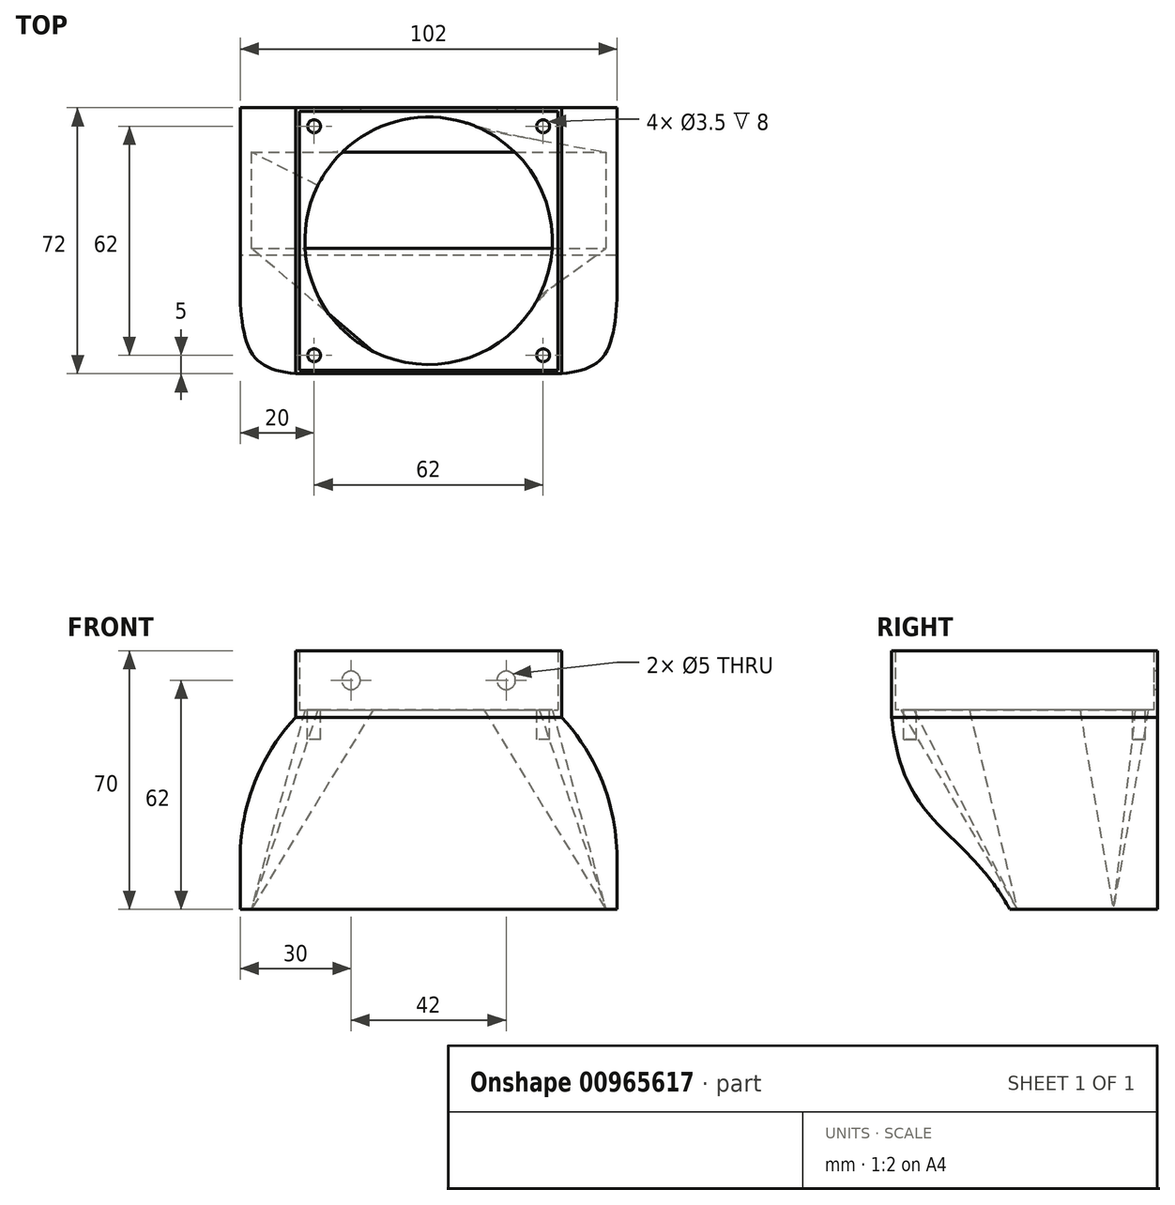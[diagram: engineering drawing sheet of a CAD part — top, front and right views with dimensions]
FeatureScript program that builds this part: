
annotation { "Feature Type Name" : "Feature", "Feature Type Description" : "" }
export const myFeature = defineFeature(function(context is Context, id is Id, definition is map)
    precondition{}
    {
        {
            var Q0;
            Q0=qCreatedBy(makeId("Top.planeOp"),FACE);
            cPlane(context, id + "F0", {"entities" : qUnion([Q0]), "cplaneType" : CPlaneType.OFFSET, "offset" : 70 * mm, "oppositeDirection" : true, "width" : 150 * mm, "height" : 150 * mm});
        }
        {
            var Q0;
            Q0=qCreatedBy(makeId("Top.planeOp"),FACE);
            cPlane(context, id + "F1", {"entities" : qUnion([Q0]), "cplaneType" : CPlaneType.OFFSET, "offset" : 16 * mm, "oppositeDirection" : true, "width" : 150 * mm, "height" : 150 * mm});
        }
        {
            var Q0;
            Q0=qCreatedBy(id+"F1.planeOp",FACE);
            var sketch = newSketch(context, id + "F2", { "sketchPlane" : qUnion([Q0])});
            skCircle(sketch, "E0", {"center": v(0, 0) * mm, "radius": 33.5 * mm});
            skLineSegment(sketch, "E1.bottom", {"start": v(-35, 35) * mm, "end": v(35, 35) * mm});
            skLineSegment(sketch, "E1.top", {"start": v(-35, -35) * mm, "end": v(35, -35) * mm});
            skLineSegment(sketch, "E1.left", {"start": v(-35, 35) * mm, "end": v(-35, -35) * mm});
            skLineSegment(sketch, "E1.right", {"start": v(35, 35) * mm, "end": v(35, -35) * mm});
            skCircle(sketch, "E2", {"center": v(-31, 31) * mm, "radius": 2 * mm});
            skCircle(sketch, "E3", {"center": v(31, 31) * mm, "radius": 2 * mm});
            skCircle(sketch, "E4", {"center": v(31, -31) * mm, "radius": 2 * mm});
            skCircle(sketch, "E5", {"center": v(-31, -31) * mm, "radius": 2 * mm});
            skSolve(sketch);
        }
        {
            var Q0;
            Q0=qCreatedBy(makeId("Top.planeOp"),FACE);
            var sketch = newSketch(context, id + "F3", { "sketchPlane" : qUnion([Q0])});
            skLineSegment(sketch, "E6.bottom", {"start": v(-36, 36) * mm, "end": v(36, 36) * mm});
            skLineSegment(sketch, "E6.top", {"start": v(-36, -36) * mm, "end": v(36, -36) * mm});
            skLineSegment(sketch, "E6.left", {"start": v(-36, 36) * mm, "end": v(-36, -36) * mm});
            skLineSegment(sketch, "E6.right", {"start": v(36, 36) * mm, "end": v(36, -36) * mm});
            skPoint(sketch, "E6.middle", {"position": v(0, 0) * mm});
            skCircle(sketch, "E7", {"center": v(-31, 31) * mm, "radius": 1.75 * mm});
            skCircle(sketch, "E8", {"center": v(31, 31) * mm, "radius": 1.75 * mm});
            skCircle(sketch, "E9", {"center": v(31, -31) * mm, "radius": 1.75 * mm});
            skCircle(sketch, "E10", {"center": v(-31, -31) * mm, "radius": 1.75 * mm});
            skSolve(sketch);
        }
        {
            var Q0;
            Q0=qCreatedBy(id+"F0.planeOp",FACE);
            var sketch = newSketch(context, id + "F4", { "sketchPlane" : qUnion([Q0])});
            skLineSegment(sketch, "E11.bottom", {"start": v(-50, 26) * mm, "end": v(50, 26) * mm});
            skLineSegment(sketch, "E11.top", {"start": v(-50, -4) * mm, "end": v(50, -4) * mm});
            skLineSegment(sketch, "E11.left", {"start": v(-50, 26) * mm, "end": v(-50, -4) * mm});
            skLineSegment(sketch, "E11.right", {"start": v(50, 26) * mm, "end": v(50, -4) * mm});
            skLineSegment(sketch, "E12.bottom", {"start": v(-48, 24) * mm, "end": v(48, 24) * mm});
            skLineSegment(sketch, "E12.top", {"start": v(-48, -2) * mm, "end": v(48, -2) * mm});
            skLineSegment(sketch, "E12.left", {"start": v(-48, 24) * mm, "end": v(-48, -2) * mm});
            skLineSegment(sketch, "E12.right", {"start": v(48, 24) * mm, "end": v(48, -2) * mm});
            skSolve(sketch);
        }
        {
            var Q0;
            Q0=makeQuery(id+"F3.imprint","IMPRINT",FACE,{"disambiguationData":[TD([[makeQuery(id+"F3.imprint","IMPRINT",EDGE,{"derivedFrom":sQuery(id+"F3.wireOp",EDGE,"E6.bottom")}),-1.0]])]});
            extrude(context, id + "F5", {"entities" : qUnion([Q0]), "oppositeDirection" : true, "depth" : 18 * mm, "offsetDistance" : 25 * mm});
        }
        {
            var Q0;
            Q0=qCreatedBy(makeId("Right.planeOp"),FACE);
            var sketch = newSketch(context, id + "F6", { "sketchPlane" : qUnion([Q0])});
            skFitSpline(sketch, "E13", {"points": [v(-4, -70) * mm, v(-36, -18) * mm], "startDerivative": vector(-37.44, 68.12) * mm, "endDerivative": vector(-9.27, 91.12) * mm});
            skLineSegment(sketch, "E14", {"start": v(36, -18) * mm, "end": v(-36, -18) * mm});
            skLineSegment(sketch, "E15", {"start": v(-4, -70) * mm, "end": v(26, -70) * mm});
            skLineSegment(sketch, "E16", {"start": v(36, -18) * mm, "end": v(36, -70) * mm});
            skLineSegment(sketch, "E17", {"start": v(36, -70) * mm, "end": v(26, -70) * mm});
            skSolve(sketch);
        }
        {
            var Q0;
            Q0=makeQuery(id+"F2.imprint","IMPRINT",FACE,{"disambiguationData":[TD([[makeQuery(id+"F2.imprint","IMPRINT",EDGE,{"derivedFrom":sQuery(id+"F2.wireOp",EDGE,"E0")}),-1.0]])]});
            var Q1;
            Q1=makeQuery(id+"F2.imprint","IMPRINT",FACE,{"disambiguationData":[TD([[makeQuery(id+"F2.imprint","IMPRINT",EDGE,{"derivedFrom":sQuery(id+"F2.wireOp",EDGE,"E2")}),1.0]])]});
            var Q2;
            Q2=makeQuery(id+"F2.imprint","IMPRINT",FACE,{"disambiguationData":[TD([[makeQuery(id+"F2.imprint","IMPRINT",EDGE,{"derivedFrom":sQuery(id+"F2.wireOp",EDGE,"E0")}),1.0]])]});
            var Q3;
            Q3=makeQuery(id+"F2.imprint","IMPRINT",FACE,{"disambiguationData":[TD([[makeQuery(id+"F2.imprint","IMPRINT",EDGE,{"derivedFrom":sQuery(id+"F2.wireOp",EDGE,"E3")}),1.0]])]});
            var Q4;
            Q4=makeQuery(id+"F2.imprint","IMPRINT",FACE,{"disambiguationData":[TD([[makeQuery(id+"F2.imprint","IMPRINT",EDGE,{"derivedFrom":sQuery(id+"F2.wireOp",EDGE,"E4")}),1.0]])]});
            var Q5;
            Q5=makeQuery(id+"F2.imprint","IMPRINT",FACE,{"disambiguationData":[TD([[makeQuery(id+"F2.imprint","IMPRINT",EDGE,{"derivedFrom":sQuery(id+"F2.wireOp",EDGE,"E5")}),1.0]])]});
            extrude(context, id + "F7", {"entities" : qUnion([Q0, Q1, Q2, Q3, Q4, Q5]), "operationType" : NewBodyOperationType.REMOVE, "endBound" : BoundingType.THROUGH_ALL, "depth" : 16 * mm, "offsetDistance" : 25 * mm});
        }
        {
            var Q0;
            Q0 = qSketchRegion(id + "F6", true);
            extrude(context, id + "F8", {"entities" : qUnion([Q0]), "operationType" : NewBodyOperationType.ADD, "depth" : 51 * mm, "offsetDistance" : 25 * mm, "hasSecondDirection" : true, "secondDirectionOppositeDirection" : true, "secondDirectionDepth" : 51 * mm});
        }
        {
            var Q1;
            Q1=makeQuery(id+"F2.imprint","IMPRINT",FACE,{"disambiguationData":[TD([[makeQuery(id+"F2.imprint","IMPRINT",EDGE,{"derivedFrom":sQuery(id+"F2.wireOp",EDGE,"E0")}),1.0]])]});
            var Q2;
            Q2=makeQuery(id+"F4.imprint","IMPRINT",FACE,{"disambiguationData":[TD([[makeQuery(id+"F4.imprint","IMPRINT",EDGE,{"derivedFrom":sQuery(id+"F4.wireOp",EDGE,"E12.bottom")}),-1.0]])]});
            loft(context, id + "F9", {"operationType" : NewBodyOperationType.REMOVE, "sheetProfilesArray" : [{ "sheetProfileEntities" : qUnion([Q1]) }, { "sheetProfileEntities" : qUnion([Q2]) }]});
        }
        {
            var Q0;
            Q0=qCreatedBy(makeId("Front.planeOp"),FACE);
            var sketch = newSketch(context, id + "F10", { "sketchPlane" : qUnion([Q0])});
            skCircle(sketch, "E18", {"center": v(-21, -8) * mm, "radius": 2.5 * mm});
            skCircle(sketch, "E19", {"center": v(21, -8) * mm, "radius": 2.5 * mm});
            skSolve(sketch);
        }
        {
            var Q0;
            Q0=makeQuery(id+"F10.imprint","IMPRINT",FACE,{"disambiguationData":[TD([[makeQuery(id+"F10.imprint","IMPRINT",EDGE,{"derivedFrom":sQuery(id+"F10.wireOp",EDGE,"E18")}),1.0]])]});
            var Q1;
            Q1=makeQuery(id+"F10.imprint","IMPRINT",FACE,{"disambiguationData":[TD([[makeQuery(id+"F10.imprint","IMPRINT",EDGE,{"derivedFrom":sQuery(id+"F10.wireOp",EDGE,"E19")}),1.0]])]});
            extrude(context, id + "F11", {"entities" : qUnion([Q0, Q1]), "operationType" : NewBodyOperationType.REMOVE, "endBound" : BoundingType.THROUGH_ALL, "oppositeDirection" : true, "depth" : 25 * mm, "offsetDistance" : 25 * mm});
        }
        {
            var Q0;
            Q0=makeQuery(id+"F3.imprint","IMPRINT",FACE,{"disambiguationData":[TD([[makeQuery(id+"F3.imprint","IMPRINT",EDGE,{"derivedFrom":sQuery(id+"F3.wireOp",EDGE,"E7")}),1.0]])]});
            var Q1;
            Q1=makeQuery(id+"F3.imprint","IMPRINT",FACE,{"disambiguationData":[TD([[makeQuery(id+"F3.imprint","IMPRINT",EDGE,{"derivedFrom":sQuery(id+"F3.wireOp",EDGE,"E8")}),1.0]])]});
            var Q2;
            Q2=makeQuery(id+"F3.imprint","IMPRINT",FACE,{"disambiguationData":[TD([[makeQuery(id+"F3.imprint","IMPRINT",EDGE,{"derivedFrom":sQuery(id+"F3.wireOp",EDGE,"E10")}),1.0]])]});
            var Q3;
            Q3=makeQuery(id+"F3.imprint","IMPRINT",FACE,{"disambiguationData":[TD([[makeQuery(id+"F3.imprint","IMPRINT",EDGE,{"derivedFrom":sQuery(id+"F3.wireOp",EDGE,"E9")}),1.0]])]});
            extrude(context, id + "F12", {"entities" : qUnion([Q0, Q1, Q2, Q3]), "operationType" : NewBodyOperationType.REMOVE, "oppositeDirection" : true, "depth" : 24 * mm, "offsetDistance" : 25 * mm});
        }
        {
            var Q0;
            Q0=makeQuery(id+"F8.opExtrude","CAP_EDGE",EDGE,{"disambiguationData":[OSD([sQuery(id+"F6.wireOp",EDGE,"E14")])],"isStart":true});
            var Q1;
            Q1=makeQuery(id+"F8.opExtrude","CAP_EDGE",EDGE,{"disambiguationData":[OSD([sQuery(id+"F6.wireOp",EDGE,"E14")])],"isStart":false});
            fillet(context, id + "F13", {"entities" : qUnion([Q0, Q1]), "radius" : 56 * mm, "tangentPropagation" : true, "allowEdgeOverflow" : false});
        }
    });
